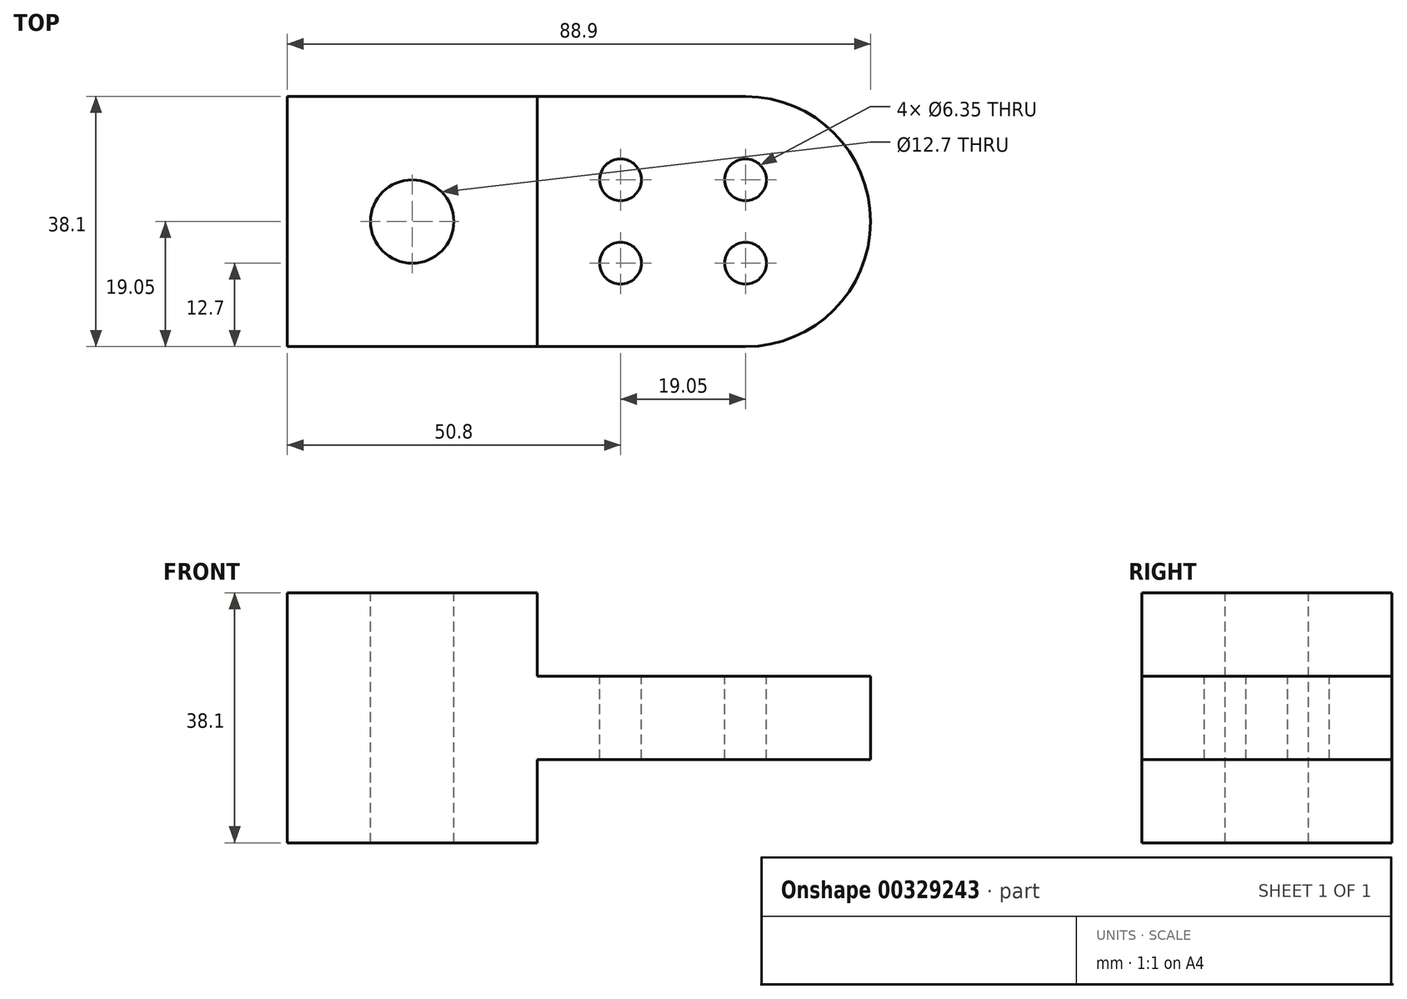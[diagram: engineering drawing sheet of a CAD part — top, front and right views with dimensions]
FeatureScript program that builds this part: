
annotation { "Feature Type Name" : "Feature", "Feature Type Description" : "" }
export const myFeature = defineFeature(function(context is Context, id is Id, definition is map)
    precondition{}
    {
        {
            var Q0;
            Q0=qCreatedBy(makeId("Front.planeOp"),FACE);
            var sketch = newSketch(context, id + "F0", { "sketchPlane" : qUnion([Q0])});
            skLineSegment(sketch, "E0", {"start": v(0, -19.05) * mm, "end": v(0, 19.05) * mm});
            skLineSegment(sketch, "E1", {"start": v(0, 19.05) * mm, "end": v(38.1, 19.05) * mm});
            skLineSegment(sketch, "E2", {"start": v(38.1, 19.05) * mm, "end": v(38.1, 6.35) * mm});
            skLineSegment(sketch, "E3", {"start": v(38.1, 6.35) * mm, "end": v(88.9, 6.35) * mm});
            skLineSegment(sketch, "E4", {"start": v(88.9, 6.35) * mm, "end": v(88.9, -6.35) * mm});
            skLineSegment(sketch, "E5", {"start": v(88.9, -6.35) * mm, "end": v(38.1, -6.35) * mm});
            skLineSegment(sketch, "E6", {"start": v(38.1, -6.35) * mm, "end": v(38.1, -19.05) * mm});
            skLineSegment(sketch, "E7", {"start": v(38.1, -19.05) * mm, "end": v(0, -19.05) * mm});
            skPoint(sketch, "E8", {"position": v(0, 0) * mm});
            skPoint(sketch, "E9", {"position": v(88.9, 0) * mm});
            skSolve(sketch);
        }
        {
            var Q0;
            Q0 = qSketchRegion(id + "F0", true);
            extrude(context, id + "F1", {"entities" : qUnion([Q0]), "depth" : 38.1 * mm});
        }
        {
            var Q0;
            Q0=makeQuery(id+"F1.opExtrude","SWEPT_FACE",FACE,{"disambiguationData":[OSD([sQuery(id+"F0.wireOp",EDGE,"E1")])]});
            var sketch = newSketch(context, id + "F2", { "sketchPlane" : qUnion([Q0])});
            skCircle(sketch, "E10", {"center": v(19.05, -19.05) * mm, "radius": 6.35 * mm});
            skCircle(sketch, "E11", {"center": v(50.8, -12.7) * mm, "radius": 3.18 * mm});
            skCircle(sketch, "E12.0.1.0", {"center": v(50.8, -25.4) * mm, "radius": 3.18 * mm});
            skCircle(sketch, "E12.1.0.0", {"center": v(69.85, -12.7) * mm, "radius": 3.18 * mm});
            skCircle(sketch, "E12.1.1.0", {"center": v(69.85, -25.4) * mm, "radius": 3.18 * mm});
            skLineSegment(sketch, "E12.direction1", {"start": v(50.8, -12.7) * mm, "end": v(69.85, -12.7) * mm, "construction": true});
            skLineSegment(sketch, "E12.direction2", {"start": v(50.8, -12.7) * mm, "end": v(50.8, -25.4) * mm, "construction": true});
            skSolve(sketch);
        }
        {
            var Q0;
            Q0=sQuery(id+"F2.wireOp",VERTEX,"E12.direction2.end");
            var Q1;
            Q1=sQuery(id+"F2.wireOp",VERTEX,"E11.center");
            var Q2;
            Q2=sQuery(id+"F2.wireOp",VERTEX,"E12.direction1.end");
            var Q3;
            Q3=sQuery(id+"F2.wireOp",VERTEX,"E12.1.1.0.center");
            var Q4;
            Q4=makeQuery(id+"F1.opExtrude","SWEPT_BODY",BODY,{"disambiguationData":[OSD([sQuery(id+"F0.wireOp",EDGE,"E0"),sQuery(id+"F0.wireOp",EDGE,"E1"),sQuery(id+"F0.wireOp",EDGE,"E2"),sQuery(id+"F0.wireOp",EDGE,"E3"),sQuery(id+"F0.wireOp",EDGE,"E4"),sQuery(id+"F0.wireOp",EDGE,"E5"),sQuery(id+"F0.wireOp",EDGE,"E6"),sQuery(id+"F0.wireOp",EDGE,"E7")])]});
            hole(context, id + "F3", {"style" : HoleStyle.SIMPLE, "endStyle" : HoleEndStyle.THROUGH, "holeDiameter" : 6.35 * mm, "tappedDepth" : 12.7 * mm, "tapClearance" : 3, "locations" : qUnion([Q0, Q1, Q2, Q3]), "scope" : qUnion([Q4])});
        }
        {
            var Q0;
            Q0=sQuery(id+"F2.wireOp",VERTEX,"E10.center");
            var Q1;
            Q1=makeQuery(id+"F1.opExtrude","SWEPT_BODY",BODY,{"disambiguationData":[OSD([sQuery(id+"F0.wireOp",EDGE,"E0"),sQuery(id+"F0.wireOp",EDGE,"E1"),sQuery(id+"F0.wireOp",EDGE,"E2"),sQuery(id+"F0.wireOp",EDGE,"E3"),sQuery(id+"F0.wireOp",EDGE,"E4"),sQuery(id+"F0.wireOp",EDGE,"E5"),sQuery(id+"F0.wireOp",EDGE,"E6"),sQuery(id+"F0.wireOp",EDGE,"E7")])]});
            hole(context, id + "F4", {"style" : HoleStyle.SIMPLE, "endStyle" : HoleEndStyle.THROUGH, "holeDiameter" : 12.7 * mm, "tappedDepth" : 12.7 * mm, "tapClearance" : 3, "locations" : qUnion([Q0]), "scope" : qUnion([Q1])});
        }
        {
            var Q0;
            Q0=makeQuery(id+"F1.opExtrude","SWEPT_FACE",FACE,{"disambiguationData":[OSD([sQuery(id+"F0.wireOp",EDGE,"E3")])]});
            var sketch = newSketch(context, id + "F5", { "sketchPlane" : qUnion([Q0])});
            skArc(sketch, "E13.MirrorCS", {"start": v(69.85, -38.1) * mm, "mid": v(88.9, -19.05) * mm, "end": v(69.85, 0) * mm});
            skPoint(sketch, "E14", {"position": v(88.9, -19.05) * mm});
            skLineSegment(sketch, "E15", {"start": v(69.85, 0) * mm, "end": v(88.9, 0) * mm});
            skLineSegment(sketch, "E16", {"start": v(88.9, 0) * mm, "end": v(88.9, -38.1) * mm});
            skLineSegment(sketch, "E17", {"start": v(88.9, -38.1) * mm, "end": v(69.85, -38.1) * mm});
            skSolve(sketch);
        }
        {
            var Q0;
            {var subQ0=sQuery(id+"F5.wireOp",EDGE,"E15");Q0=makeQuery(id+"F5.imprint","IMPRINT",FACE,{"disambiguationData":[TD([[makeQuery(id+"F5.imprint","IMPRINT",EDGE,{"derivedFrom":subQ0}),-1.0]])]});}
            extrude(context, id + "F6", {"entities" : qUnion([Q0]), "operationType" : NewBodyOperationType.REMOVE, "oppositeDirection" : true, "depth" : 25.4 * mm});
        }
        {
            var Q0;
            {var subQ0=sQuery(id+"F5.wireOp",EDGE,"E17");Q0=makeQuery(id+"F5.imprint","IMPRINT",FACE,{"disambiguationData":[TD([[makeQuery(id+"F5.imprint","IMPRINT",EDGE,{"derivedFrom":subQ0}),1.0]])]});}
            extrude(context, id + "F7", {"entities" : qUnion([Q0]), "operationType" : NewBodyOperationType.REMOVE, "oppositeDirection" : true, "depth" : 25.4 * mm});
        }
    });
